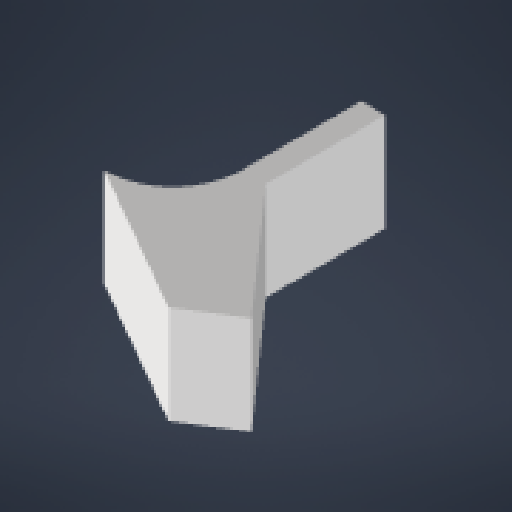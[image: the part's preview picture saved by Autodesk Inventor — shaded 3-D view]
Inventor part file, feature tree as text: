
AUTODESK INVENTOR PART (.ipt)
format: ipt  version: 2024 (Build 280153000, 153)  size: 240,640 bytes
history: native  units: mm
features: other x10, reference x10, extrude x6, sketch x6, fillet x3, chamfer x2
ambient origin geometry x8: Origin, YZ Plane, XZ Plane, XY Plane, X Axis, Y Axis, Z Axis, Center Point
bodies: Body1 (feature_tree)
feature tree (37):
  other  "Твердое тело1"
  extrude  "Выдавливание1"  Depth=28.75mm TaperAngle=0.0deg
  other  "РабПлоскость2"
  extrude  "Выдавливание4"  Depth=5.0mm
  fillet  "Сопряжение1"  Radius=20.0mm
  extrude  "Выдавливание5"  Depth=80.0mm
  extrude  "Выдавливание6"  Depth=25.0mm
  extrude  "Выдавливание7"  Depth=80.0mm
  fillet  "Сопряжение2"  Radius=50.0mm
  extrude  "Выдавливание8"  Depth=85.0mm TaperAngle=0.0deg
  fillet  "Сопряжение3"  Radius=15.0mm
  chamfer  "Фаска1"  Distance=3.0mm
  chamfer  "Фаска2"  Distance=5.5mm
  sketch  "Эскиз1"
  reference  "Ссылка1"
  reference  "Ссылка2"
  reference  "Ссылка3"
  reference  "Ссылка4"
  reference  "Ссылка5"
  sketch  "Эскиз4"
  reference  "Ссылка8"
  reference  "Ссылка9"
  sketch  "Эскиз6"
  sketch  "Эскиз7"
  reference  "Ссылка10"
  sketch  "Эскиз8"
  sketch  "Эскиз9"
  reference  "Ссылка11"
  reference  "Ссылка12"
  parser-record x1  (decoder bookkeeping rows leaked as tree rows — omitted from the tree; the rows remain in map.json)
  other  "main_assembly.iam"
  other  "manipulator:1"
  other  "platform:2"
  other  "base_assambly:1"
  other  "fb_axis:2"
  other  "arm_assembly_l:2"
  other  "motor_holder_l:1"
note: 1 file-system path scrubbed to <path> (originals preserved in map.json)
